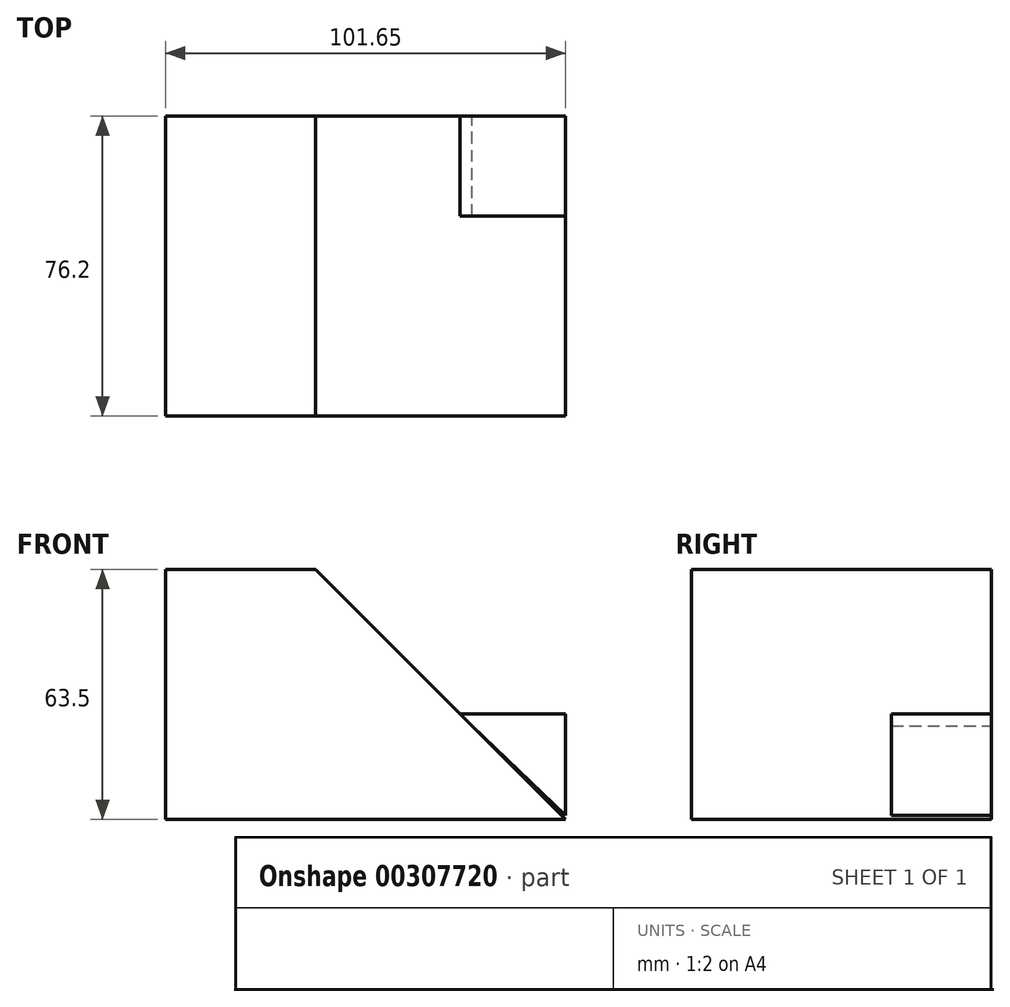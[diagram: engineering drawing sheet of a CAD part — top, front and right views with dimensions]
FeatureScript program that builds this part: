
annotation { "Feature Type Name" : "Feature", "Feature Type Description" : "" }
export const myFeature = defineFeature(function(context is Context, id is Id, definition is map)
    precondition{}
    {
        {
            var Q0;
            Q0=qCreatedBy(makeId("Front.planeOp"),FACE);
            var sketch = newSketch(context, id + "F0", { "sketchPlane" : qUnion([Q0])});
            skLineSegment(sketch, "E0", {"start": v(-10.35, 23.5) * mm, "end": v(27.75, 23.5) * mm});
            skLineSegment(sketch, "E1", {"start": v(27.75, 23.5) * mm, "end": v(91.25, -40) * mm});
            skLineSegment(sketch, "E2", {"start": v(91.25, -40) * mm, "end": v(-10.35, -40) * mm});
            skLineSegment(sketch, "E3", {"start": v(-10.35, -40) * mm, "end": v(-10.35, 23.5) * mm});
            skSolve(sketch);
        }
        {
            var Q0;
            Q0 = qSketchRegion(id + "F0", true);
            extrude(context, id + "F1", {"entities" : qUnion([Q0]), "depth" : 76.2 * mm});
        }
        {
            var Q0;
            Q0=qCreatedBy(makeId("Front.planeOp"),FACE);
            var sketch = newSketch(context, id + "F2", { "sketchPlane" : qUnion([Q0])});
            skLineSegment(sketch, "E4", {"start": v(64.35, -13.23) * mm, "end": v(91.3, -13.23) * mm});
            skLineSegment(sketch, "E5", {"start": v(91.3, -13.23) * mm, "end": v(91.3, -38.97) * mm});
            skLineSegment(sketch, "E6", {"start": v(91.3, -38.97) * mm, "end": v(64.35, -13.23) * mm});
            skSolve(sketch);
        }
        {
            var Q0;
            Q0 = qSketchRegion(id + "F2", true);
            extrude(context, id + "F3", {"entities" : qUnion([Q0]), "operationType" : NewBodyOperationType.ADD, "depth" : 25.4 * mm});
        }
    });
